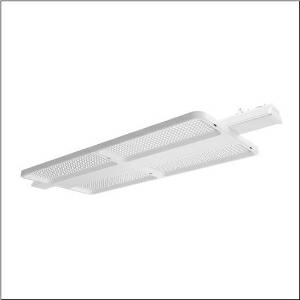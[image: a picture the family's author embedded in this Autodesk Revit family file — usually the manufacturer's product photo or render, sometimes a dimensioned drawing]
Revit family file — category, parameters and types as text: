
# Revit family: highbay_21_fur_licross_r__tragschiene_maxi_52hn11db5qla_b855
name_source: partatom
category: Lighting Fixtures
units: mm (PartAtom-declared; Revit-internal decimal feet)

## family parameters
Cut with Voids When Loaded = No
Host = Face
Light Source = No
Part Type = Normal
Room Calculation Point = No
Round Connector Dimension = Use Diameter
Shared = No

## types (1)
- --- (1 x LED, 5680 lm, 31.4 W, 5000K)
    Apparent Load = 31 VA
    CIE Flux Codes = 89 97 99 100 100
    Color Rendering = 80
    Color Temperature = 5000K
    Default Elevation = 1800 mm
    Description = high bay luminaire Highbay 21 for Licross® trunking rail maxi; direct symmetric narrow distribution, light control with lens of PMMA; UGR ≤ 22 (X = 4H | Y = 8H | S = 0.25H | reflection values 70/50/20); luminous flux: 36.980lm; light colour: 850, colour temperature: 5000K, MacAdam ≤ 3 SDCM (initial), colour rendering: CRI > 80; luminous efficacy: 187,1lm/W; rated service life: 75.000h (L80/B50) at AT= ta max; control: DALI 2; luminaire connection: plug, 5-pole, with phase selectionmains connection: 230..240V, AC 50/60Hz; connected load: 197,7W; protection rating (complete): IP64; insulation class (complete): insulation class I (protective earthing); protection symbol: D; impact resistance: IK07; certification: CE, ENEC, VDE, UKCA; internal wiring halogen-free; luminaire corresponds to IFS (International Featured Standards) requirements for safety and quality in the food industry; LABS conformity tested according to VDMA 24364:2018-05; housing frame of high-performance plastic PA6, matt traffic white (RAL 9016); cover of PMMA; fixing on rail side of steel, galvanised, white; blank cover of PC/ABS, traffic white (RAL 9016); dimension (LxWxH): 1.250 x 442 x 71mm; permissible operating ambient temperature: -40..+55°C (reducing of maximum allowable ambient temperature of 5°C with ceiling mounting); packaging unit: 1 piece
    Height = 72 mm  [stored 0.23622 ft]
    Lamp = 1 x LED
    Lamp Light Flux = 5680 lm
    Lamp Power = 31.4 W
    Lamp count = 1
    Length = 946 mm
    Luminous efficacy = 181 lm/W
    Manufacturer = Siteco
    ModVariant = No
    Model = 52HN11DB5QLA
    Mounting Place = Ceiling
    Mounting Type = Pendant
    Number of Poles = 1
    OnlyDefault = Yes
    Power Factor = 1
    Product Name = Highbay 21 für Licross® Tragschiene maxi
    Product group = high bay luminaire
    ProductGroupID = 901
    Protection Class = Protection class I
    Protection Degree = IP 64
    RLX_Detail_Level = 1
    RLX_Emergency_Light_Flux = 0 lm
    RLX_Emergency_Type = 0
    RLX_Emergency_Type_DB = No
    RlxData = <blob elided: 130369 chars, md5=6b8df1d0>
    Socket = socket
    Standby Power = 0 W
    System Light Flux = 5680 lm
    System Power = 31 W
    Type Comments = : DC mode (central or group accumulator) initial emergency light level
    Type Image = l_1361711.jpg
    URL = http://relux.com
    VarID = @adj_000989
    Voltage = 0 V
    Weight = 0.00 kg
    Width = 442 mm

note: [stored X ft] marks values corroborated as IEEE doubles in the binary element streams (Revit-internal decimal feet)

## geometry (parser evidence)
native form markers: Blend x4, Sweep x10
no freeform markers — native parametric forms only
